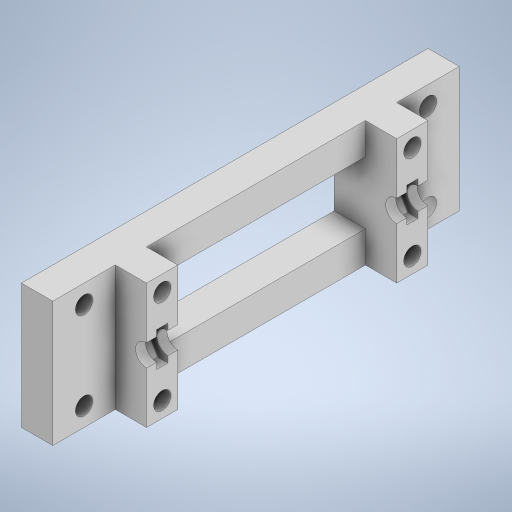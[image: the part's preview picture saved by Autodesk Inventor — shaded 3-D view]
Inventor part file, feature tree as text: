
AUTODESK INVENTOR PART (.ipt)
format: ipt  version: 2023 (Build 270158000, 158)  size: 373,248 bytes
history: native  units: mm
features: extrude x7, sketch x7, plane x2, mirror x1
ambient origin geometry x8: Origin, YZ Plane, XZ Plane, XY Plane, X Axis, Y Axis, Z Axis, Center Point
bodies: Solid1 (feature_tree)
feature tree (17):
  extrude  "Extrusion1"  Depth=5.0mm
  extrude  "Extrusion2"  Depth=15.0mm
  extrude  "Extrusion3"  Depth=35.0mm
  extrude  "Extrusion4"  Depth=10.0mm
  extrude  "Extrusion5"  Depth=10.0mm
  extrude  "Extrusion6"  Depth=200.0mm TaperAngle=0.0deg
  plane  "Work Plane1"
  extrude  "Extrusion7"  Depth=5.0mm
  plane  "Work Plane2"
  mirror  "Mirror1"
  sketch  "Sketch1"  dims[d0=5.0mm d1=5.0mm]
  sketch  "Sketch2"  dims[d2=5.0mm d3=15.0mm]
  sketch  "Sketch3"  dims[d4=15.0mm d5=35.0mm]
  sketch  "Sketch4"  dims[d6=20.0mm d7=0.0mm d8=10.0mm]
  sketch  "Sketch5"  dims[d9=10.0mm d10=10.0mm]
  sketch  "Sketch6"  dims[d11=3.5mm d12=200.0mm d13=0.0mm]
  sketch  "Sketch7"  dims[d14=5.0mm d15=5.0mm d16=20.0mm d17=0.0mm d18=10.0mm d19=10.0mm d20=3.0mm d21=3.0mm d22=5.0mm d23=5.0mm d24=5.0mm d25=5.0mm d26=3.0mm d27=3.0mm d28=2.75mm d29=2.75mm d30=2.75mm d31=2.75mm d32=5.0mm d33=0.0mm d34=2.5mm d35=2.5mm d36=2.5mm d37=2.5mm d38=2.5mm d39=2.5mm d40=2.5mm d41=2.5mm d42=2.75mm d43=2.75mm d44=2.75mm d45=2.75mm d46=15.0mm d47=0.0mm d48=4.0mm d49=4.0mm d50=4.0mm d51=4.0mm d52=5.0mm d53=0.0mm d54=2.75mm d55=0.0mm d56=10.0mm d57=20.0mm d58=1.8mm d59=0.0mm]
